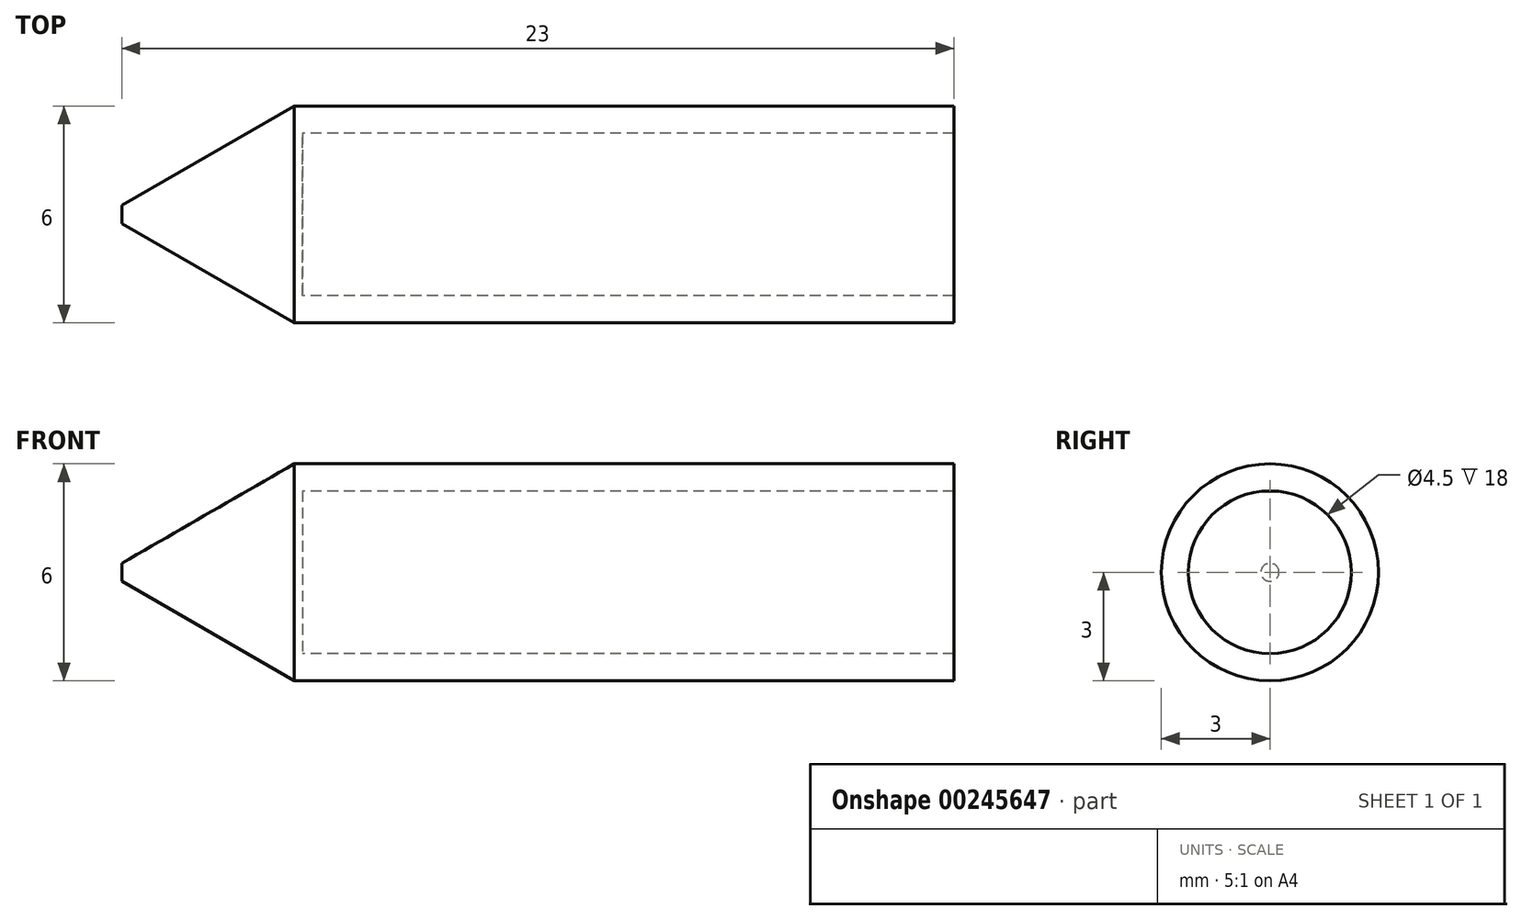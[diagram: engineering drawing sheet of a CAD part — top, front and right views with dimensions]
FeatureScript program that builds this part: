
annotation { "Feature Type Name" : "Feature", "Feature Type Description" : "" }
export const myFeature = defineFeature(function(context is Context, id is Id, definition is map)
    precondition{}
    {
        {
            var Q0;
            Q0=qCreatedBy(makeId("Front.planeOp"),FACE);
            var sketch = newSketch(context, id + "F0", { "sketchPlane" : qUnion([Q0])});
            skLineSegment(sketch, "E0", {"start": v(0, 2.25) * mm, "end": v(0, 3) * mm});
            skLineSegment(sketch, "E1", {"start": v(-18, 0) * mm, "end": v(-23, 0) * mm, "construction": true});
            skLineSegment(sketch, "E2", {"start": v(-23, 0) * mm, "end": v(-23, 0.25) * mm});
            skLineSegment(sketch, "E3", {"start": v(-23, 0.25) * mm, "end": v(-18.24, 3) * mm});
            skLineSegment(sketch, "E4", {"start": v(-23, 0) * mm, "end": v(-18, 0) * mm});
            skLineSegment(sketch, "E5", {"start": v(-18, 0) * mm, "end": v(-18, 2.25) * mm});
            skLineSegment(sketch, "E6", {"start": v(-18, 2.25) * mm, "end": v(0, 2.25) * mm});
            skLineSegment(sketch, "E7", {"start": v(0, 3) * mm, "end": v(-18.24, 3) * mm});
            skSolve(sketch);
        }
        {
            var Q0;
            Q0=makeQuery(id+"F0.imprint","IMPRINT",FACE,{"disambiguationData":[TD([[makeQuery(id+"F0.imprint","IMPRINT",EDGE,{"derivedFrom":sQuery(id+"F0.wireOp",EDGE,"E0")}),1.0]])]});
            var Q1;
            Q1=sQuery(id+"F0.wireOp",EDGE,"E4");
            revolve(context, id + "F1", {"surfaceOperationType" : NewSurfaceOperationType.NEW, "entities" : qUnion([Q0]), "axis" : qUnion([Q1]), "revolveType" : RevolveType.FULL});
        }
    });
